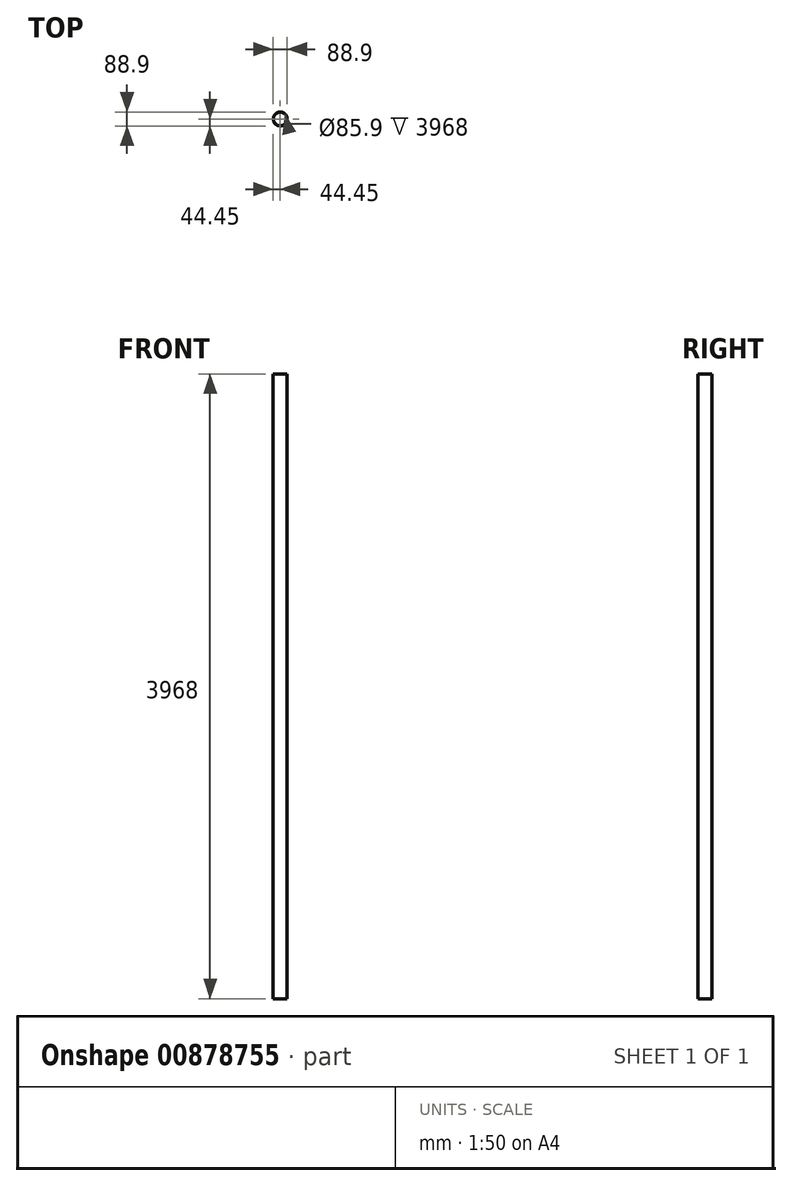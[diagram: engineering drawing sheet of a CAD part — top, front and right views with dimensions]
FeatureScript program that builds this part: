
annotation { "Feature Type Name" : "Feature", "Feature Type Description" : "" }
export const myFeature = defineFeature(function(context is Context, id is Id, definition is map)
    precondition{}
    {
        {
            var Q0;
            Q0=qCreatedBy(makeId("Top.planeOp"),FACE);
            var sketch = newSketch(context, id + "F0", { "sketchPlane" : qUnion([Q0])});
            skCircle(sketch, "E0", {"center": v(0, 0) * mm, "radius": 44.45 * mm});
            skCircle(sketch, "E1", {"center": v(0, 0) * mm, "radius": 42.95 * mm});
            skSolve(sketch);
        }
        {
            var Q0;
            Q0=makeQuery(id+"F0.imprint","IMPRINT",FACE,{"disambiguationData":[TD([[makeQuery(id+"F0.imprint","IMPRINT",EDGE,{"derivedFrom":sQuery(id+"F0.wireOp",EDGE,"E0")}),1.0]])]});
            extrude(context, id + "F1", {"entities" : qUnion([Q0]), "depth" : 3968 * mm, "offsetDistance" : 25 * mm});
        }
    });
